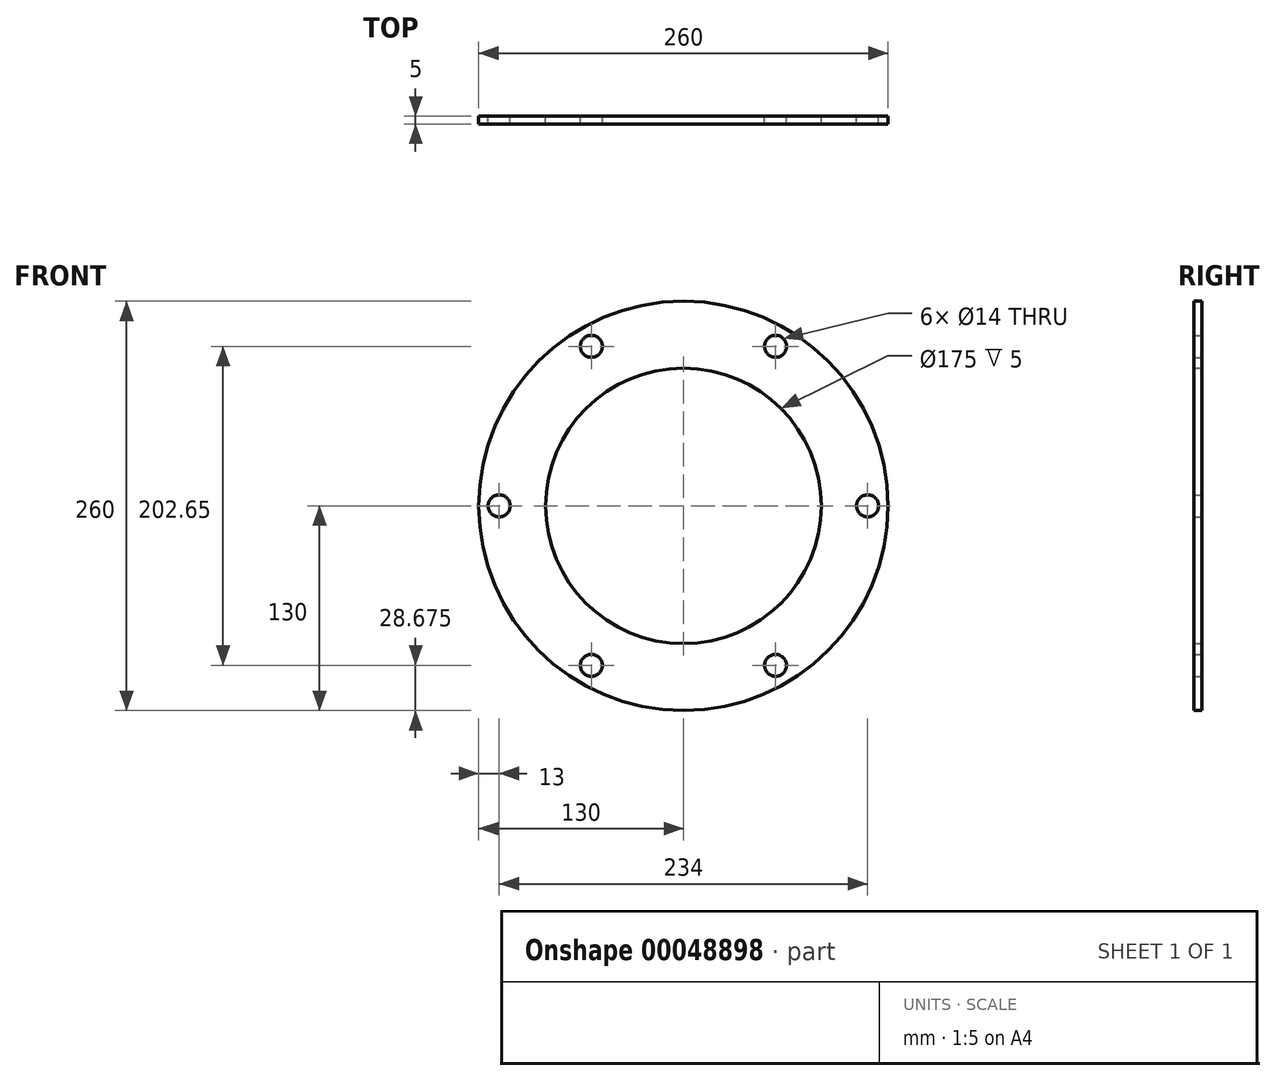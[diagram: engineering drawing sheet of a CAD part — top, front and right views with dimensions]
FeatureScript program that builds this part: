
annotation { "Feature Type Name" : "Feature", "Feature Type Description" : "" }
export const myFeature = defineFeature(function(context is Context, id is Id, definition is map)
    precondition{}
    {
        {
            var Q0;
            Q0=qCreatedBy(makeId("Front.planeOp"),FACE);
            var sketch = newSketch(context, id + "F0", { "sketchPlane" : qUnion([Q0])});
            skCircle(sketch, "E0", {"center": v(0, 0) * mm, "radius": 130 * mm});
            skCircle(sketch, "E1", {"center": v(0, 0) * mm, "radius": 87.5 * mm});
            skCircle(sketch, "E2", {"center": v(0, 0) * mm, "radius": 124 * mm, "construction": true});
            skCircle(sketch, "E3", {"center": v(0, 0) * mm, "radius": 110 * mm, "construction": true});
            skLineSegment(sketch, "E4", {"start": v(0, 0) * mm, "end": v(-110, 0) * mm, "construction": true});
            skLineSegment(sketch, "E5", {"start": v(-110, 0) * mm, "end": v(-124, 0) * mm, "construction": true});
            skCircle(sketch, "E6", {"center": v(-117, 0) * mm, "radius": 7 * mm});
            skCircle(sketch, "E7.1.0", {"center": v(-58.5, -101.32) * mm, "radius": 7 * mm});
            skCircle(sketch, "E7.2.0", {"center": v(58.5, -101.32) * mm, "radius": 7 * mm});
            skCircle(sketch, "E7.3.0", {"center": v(117, 0) * mm, "radius": 7 * mm});
            skCircle(sketch, "E7.4.0", {"center": v(58.5, 101.32) * mm, "radius": 7 * mm});
            skCircle(sketch, "E7.5.0", {"center": v(-58.5, 101.32) * mm, "radius": 7 * mm});
            skSolve(sketch);
        }
        {
            var Q0;
            Q0=makeQuery(id+"F0.imprint","IMPRINT",FACE,{"disambiguationData":[TD([[makeQuery(id+"F0.imprint","IMPRINT",EDGE,{"derivedFrom":sQuery(id+"F0.wireOp",EDGE,"E0")}),1.0]])]});
            extrude(context, id + "F1", {"entities" : qUnion([Q0]), "depth" : 5 * mm});
        }
    });
